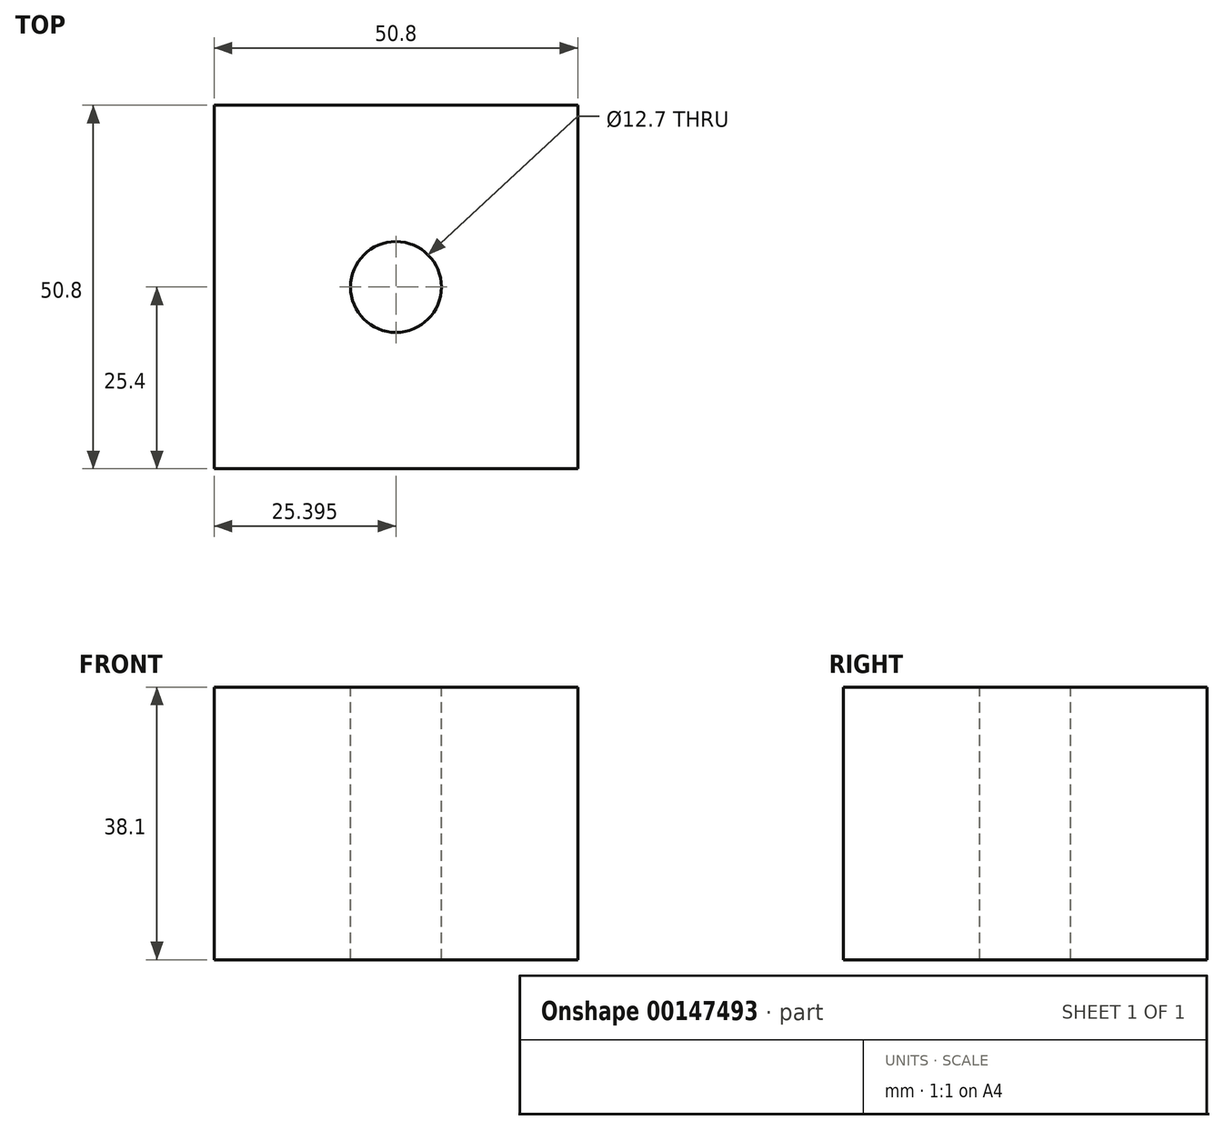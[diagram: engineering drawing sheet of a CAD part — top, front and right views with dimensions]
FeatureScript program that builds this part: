
annotation { "Feature Type Name" : "Feature", "Feature Type Description" : "" }
export const myFeature = defineFeature(function(context is Context, id is Id, definition is map)
    precondition{}
    {
        {
            var Q0;
            Q0=qCreatedBy(makeId("Front.planeOp"),FACE);
            var sketch = newSketch(context, id + "F0", { "sketchPlane" : qUnion([Q0])});
            skLineSegment(sketch, "E0.bottom", {"start": v(-15.61, 42.16) * mm, "end": v(35.19, 42.16) * mm});
            skLineSegment(sketch, "E0.top", {"start": v(-15.61, 4.06) * mm, "end": v(35.19, 4.06) * mm});
            skLineSegment(sketch, "E0.left", {"start": v(-15.61, 42.16) * mm, "end": v(-15.61, 4.06) * mm});
            skLineSegment(sketch, "E0.right", {"start": v(35.19, 42.16) * mm, "end": v(35.19, 4.06) * mm});
            skSolve(sketch);
        }
        {
            var Q0;
            Q0 = qSketchRegion(id + "F0", true);
            extrude(context, id + "F1", {"entities" : qUnion([Q0]), "depth" : 50.8 * mm});
        }
        {
            var Q0;
            Q0=makeQuery(id+"F1.opExtrude","SWEPT_FACE",FACE,{"disambiguationData":[OSD([sQuery(id+"F0.wireOp",EDGE,"E0.bottom")])]});
            var sketch = newSketch(context, id + "F2", { "sketchPlane" : qUnion([Q0])});
            skPoint(sketch, "E1.centerSnap0", {"position": v(-15.61, -25.4) * mm});
            skPoint(sketch, "E1.centerSnap1", {"position": v(9.79, -50.8) * mm});
            skCircle(sketch, "E2", {"center": v(9.79, -25.4) * mm, "radius": 6.35 * mm});
            skSolve(sketch);
        }
        {
            var Q0;
            Q0=makeQuery(id+"F2.imprint","IMPRINT",FACE,{"disambiguationData":[TD([[makeQuery(id+"F2.imprint","IMPRINT",EDGE,{"derivedFrom":sQuery(id+"F2.wireOp",EDGE,"E2")}),1.0]])]});
            extrude(context, id + "F3", {"entities" : qUnion([Q0]), "operationType" : NewBodyOperationType.REMOVE, "oppositeDirection" : true, "depth" : 56.52 * mm});
        }
    });
